# Revit family: 70376275-2286-4562-be80-97e4037d315e
name_source: partatom
category: Generic Models
revit_build: Autodesk Revit Architecture 2012 (Build: 20110916_2132(x64)
units: mm (PartAtom-declared; Revit-internal decimal feet)

## types (2) — shared parameters
Assembly Code = E1090900
Capacity = 1000 lbs per rung
Default Elevation = 4' - 0"
Description = UPNOVR U-301 Roof Access Caged Vertical Aluminum Ladder
Frame Material = Metal - UPNOVR - 6061-T6 Aluminum
Green Building-LEED = http://www.arcat.com
Keynote = 05510
Manufacturer = UPNOVR, Inc.
Manufacturer Website = http://www.aclindustries.com
Model = U-301
Product Data = http://www.arcat.com
Revision = R1_04-2013
Rung Spacing = 1' - 0"
Sales Information = http://www.aclindustries.com
Send Message = http://www.arcat.com
Standards Conformance = OSHA and ANSI A14.3
Top Level to Ladder Wall Bracket CL = 0' - 6"
URL = http://www.aclindustries.com
zero-valued in all types: Expected Lifespan (Years), Maintenance Schedule (Months), Warranty Duration (Years)

## per-type parameters (varying)
| type | Unit Width |
| 24"" Wide | 2' - 0" |
| 18"" Wide | 1' - 6" |

## geometry (parser evidence)
native form markers: Sweep x8
no freeform markers — native parametric forms only
